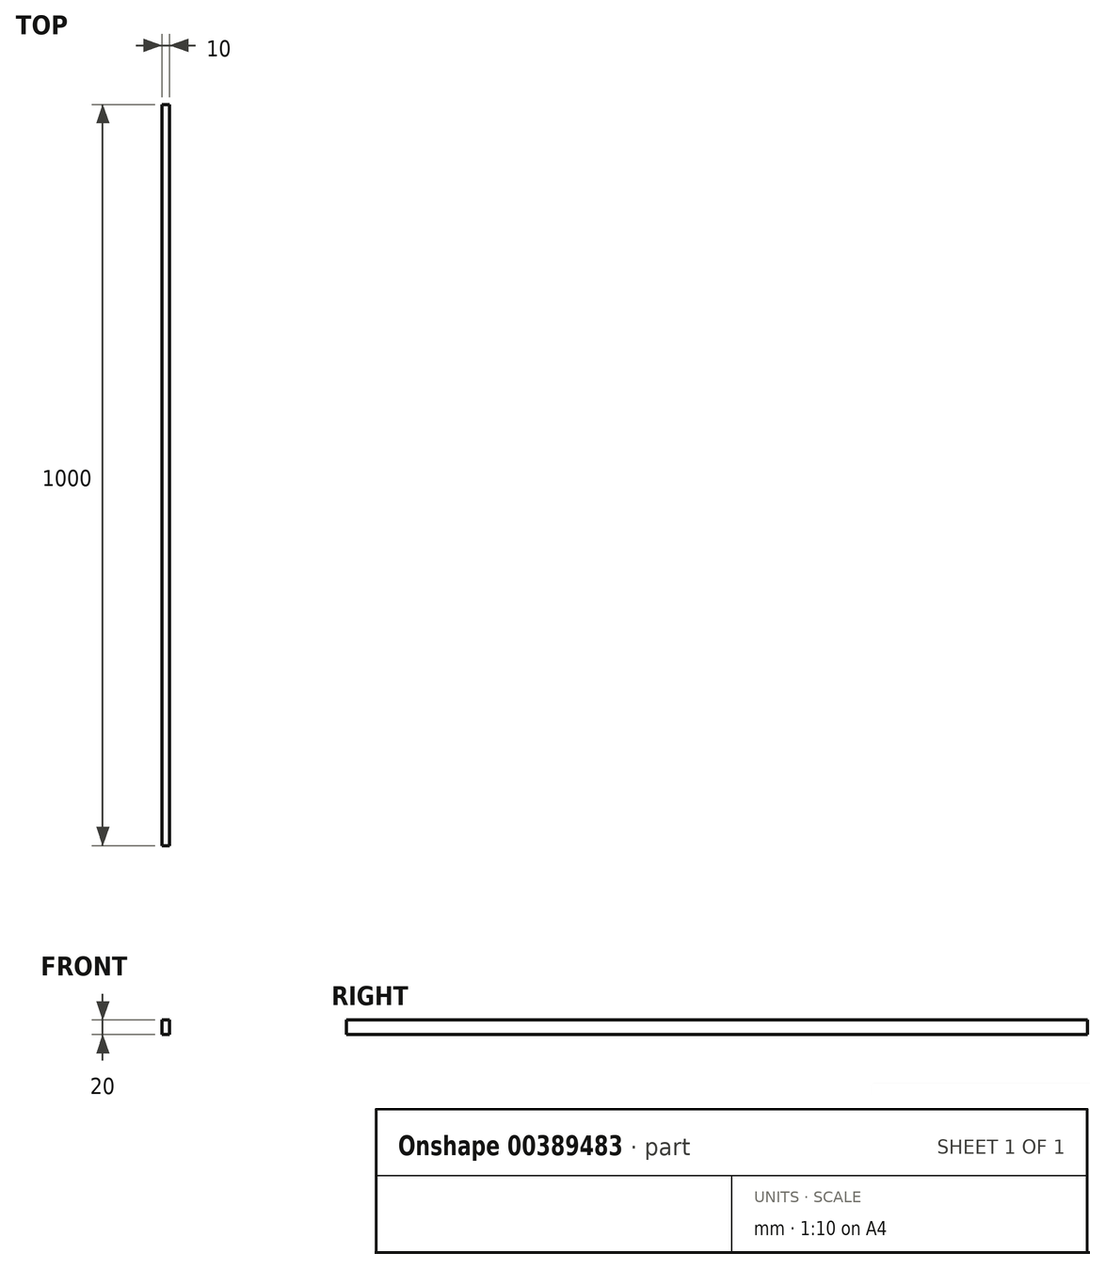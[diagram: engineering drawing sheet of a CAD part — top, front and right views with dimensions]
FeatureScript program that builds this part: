
annotation { "Feature Type Name" : "Feature", "Feature Type Description" : "" }
export const myFeature = defineFeature(function(context is Context, id is Id, definition is map)
    precondition{}
    {
        {
            var Q0;
            Q0=qCreatedBy(makeId("Front.planeOp"),FACE);
            var sketch = newSketch(context, id + "F0", { "sketchPlane" : qUnion([Q0])});
            skLineSegment(sketch, "E0.bottom", {"start": v(0, 0) * mm, "end": v(10, 0) * mm});
            skLineSegment(sketch, "E0.top", {"start": v(0, 20) * mm, "end": v(10, 20) * mm});
            skLineSegment(sketch, "E0.left", {"start": v(0, 0) * mm, "end": v(0, 20) * mm});
            skLineSegment(sketch, "E0.right", {"start": v(10, 0) * mm, "end": v(10, 20) * mm});
            skSolve(sketch);
        }
        {
            var Q0;
            Q0=makeQuery(id+"F0.imprint","IMPRINT",FACE,{"disambiguationData":[TD([[makeQuery(id+"F0.imprint","IMPRINT",EDGE,{"derivedFrom":sQuery(id+"F0.wireOp",EDGE,"E0.bottom")}),1.0]])]});
            extrude(context, id + "F1", {"entities" : qUnion([Q0]), "depth" : 1000 * mm});
        }
    });
